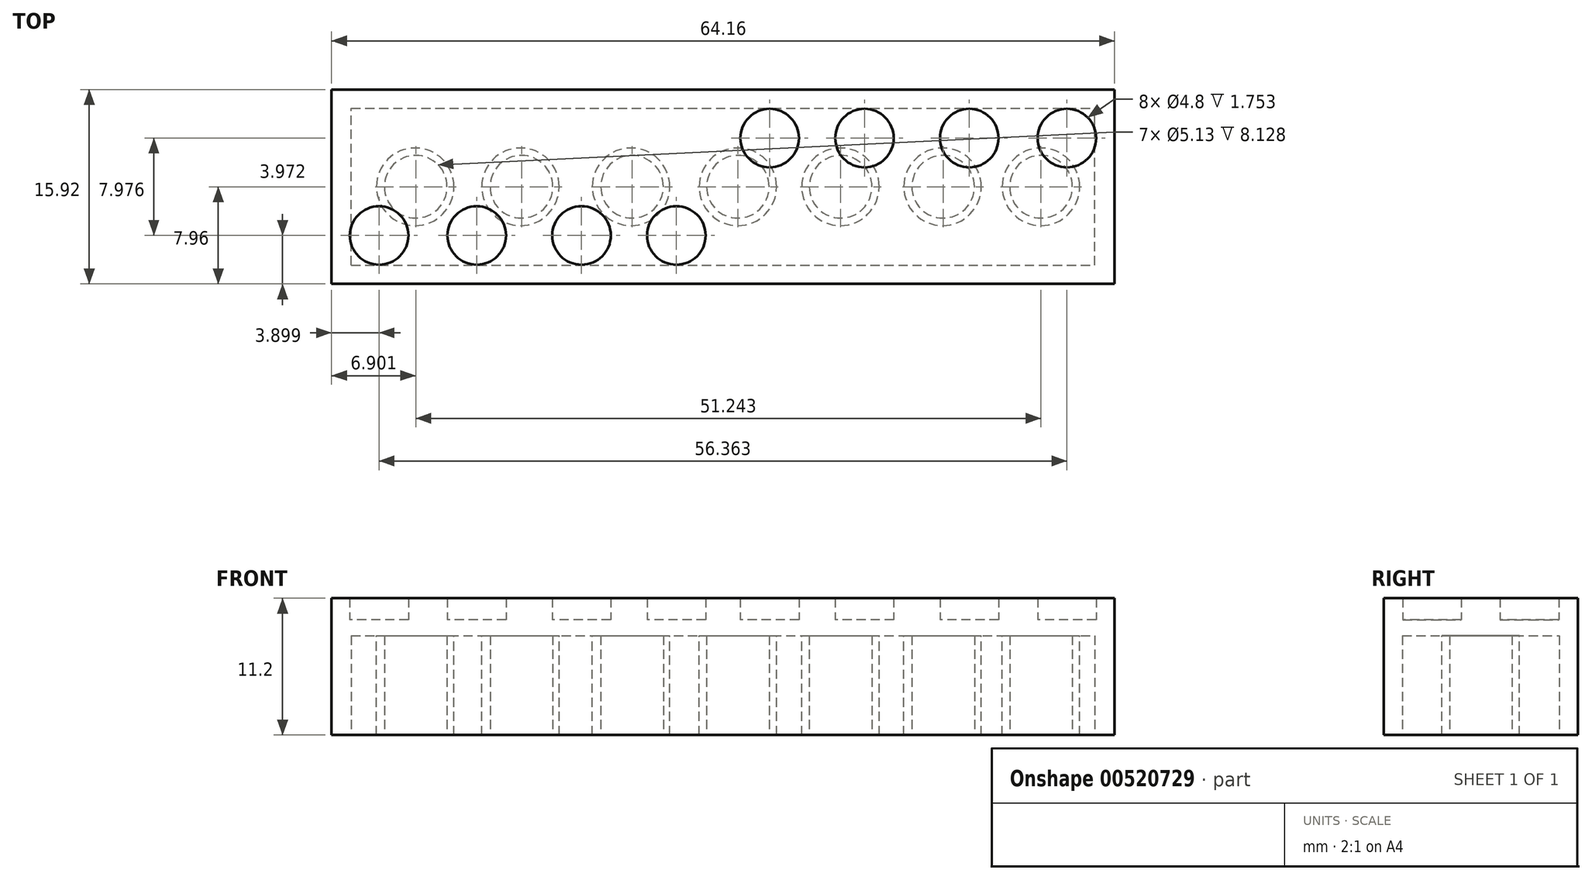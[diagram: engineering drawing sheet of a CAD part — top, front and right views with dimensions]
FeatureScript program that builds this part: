
annotation { "Feature Type Name" : "Feature", "Feature Type Description" : "" }
export const myFeature = defineFeature(function(context is Context, id is Id, definition is map)
    precondition{}
    {
        {
            var Q0;
            Q0=qCreatedBy(makeId("Top.planeOp"),FACE);
            var sketch = newSketch(context, id + "F0", { "sketchPlane" : qUnion([Q0])});
            skLineSegment(sketch, "E0.bottom", {"start": v(-32.08, 7.96) * mm, "end": v(32.08, 7.96) * mm});
            skLineSegment(sketch, "E0.top", {"start": v(-32.08, -7.96) * mm, "end": v(32.08, -7.96) * mm});
            skLineSegment(sketch, "E0.left", {"start": v(-32.08, 7.96) * mm, "end": v(-32.08, -7.96) * mm});
            skLineSegment(sketch, "E0.right", {"start": v(32.08, 7.96) * mm, "end": v(32.08, -7.96) * mm});
            skPoint(sketch, "E0.middle", {"position": v(0, 0) * mm});
            skSolve(sketch);
        }
        {
            var Q0;
            Q0=makeQuery(id+"F0.imprint","IMPRINT",FACE,{"disambiguationData":[TD([[makeQuery(id+"F0.imprint","IMPRINT",EDGE,{"derivedFrom":sQuery(id+"F0.wireOp",EDGE,"E0.bottom")}),-1.0]])]});
            extrude(context, id + "F1", {"entities" : qUnion([Q0]), "depth" : 9.45 * mm, "offsetDistance" : 25.4 * mm});
        }
        {
            var Q0;
            Q0=makeQuery(id+"F1.opExtrude","CAP_FACE",FACE,{"disambiguationData":[OSD([sQuery(id+"F0.wireOp",EDGE,"E0.bottom"),sQuery(id+"F0.wireOp",EDGE,"E0.top"),sQuery(id+"F0.wireOp",EDGE,"E0.left"),sQuery(id+"F0.wireOp",EDGE,"E0.right")])],"isStart":false});
            var sketch = newSketch(context, id + "F2", { "sketchPlane" : qUnion([Q0])});
            skCircle(sketch, "E1", {"center": v(-28.18, 3.99) * mm, "radius": 2.4 * mm});
            skCircle(sketch, "E2", {"center": v(-20.18, 3.99) * mm, "radius": 2.4 * mm});
            skCircle(sketch, "E3", {"center": v(-11.6, 3.99) * mm, "radius": 2.4 * mm});
            skCircle(sketch, "E4", {"center": v(-3.82, 3.99) * mm, "radius": 2.4 * mm});
            skCircle(sketch, "E5.MirrorC", {"center": v(3.82, 3.99) * mm, "radius": 2.4 * mm});
            skCircle(sketch, "E6.MirrorC", {"center": v(11.6, 3.99) * mm, "radius": 2.4 * mm});
            skCircle(sketch, "E7.MirrorC", {"center": v(20.18, 3.99) * mm, "radius": 2.4 * mm});
            skCircle(sketch, "E8.MirrorC", {"center": v(28.18, 3.99) * mm, "radius": 2.4 * mm});
            skCircle(sketch, "E9.MirrorC", {"center": v(28.18, -3.99) * mm, "radius": 2.4 * mm});
            skCircle(sketch, "E10.MirrorC", {"center": v(20.18, -3.99) * mm, "radius": 2.4 * mm});
            skCircle(sketch, "E11.MirrorC", {"center": v(11.6, -3.99) * mm, "radius": 2.4 * mm});
            skCircle(sketch, "E12.MirrorC", {"center": v(3.82, -3.99) * mm, "radius": 2.4 * mm});
            skCircle(sketch, "E13.MirrorC", {"center": v(-3.82, -3.99) * mm, "radius": 2.4 * mm});
            skCircle(sketch, "E14.MirrorC", {"center": v(-11.6, -3.99) * mm, "radius": 2.4 * mm});
            skCircle(sketch, "E15.MirrorC", {"center": v(-20.18, -3.99) * mm, "radius": 2.4 * mm});
            skCircle(sketch, "E16.MirrorC", {"center": v(-28.18, -3.99) * mm, "radius": 2.4 * mm});
            skSolve(sketch);
        }
        {
            var Q0;
            Q0=makeQuery(id+"F2.imprint","IMPRINT",FACE,{"disambiguationData":[TD([[makeQuery(id+"F2.imprint","IMPRINT",EDGE,{"derivedFrom":sQuery(id+"F2.wireOp",EDGE,"E16.MirrorC")}),-1.0]])]});
            var Q1;
            Q1=makeQuery(id+"F2.imprint","IMPRINT",FACE,{"disambiguationData":[TD([[makeQuery(id+"F2.imprint","IMPRINT",EDGE,{"derivedFrom":sQuery(id+"F2.wireOp",EDGE,"E15.MirrorC")}),-1.0]])]});
            var Q2;
            Q2=makeQuery(id+"F2.imprint","IMPRINT",FACE,{"disambiguationData":[TD([[makeQuery(id+"F2.imprint","IMPRINT",EDGE,{"derivedFrom":sQuery(id+"F2.wireOp",EDGE,"E14.MirrorC")}),-1.0]])]});
            var Q3;
            Q3=makeQuery(id+"F2.imprint","IMPRINT",FACE,{"disambiguationData":[TD([[makeQuery(id+"F2.imprint","IMPRINT",EDGE,{"derivedFrom":sQuery(id+"F2.wireOp",EDGE,"E13.MirrorC")}),-1.0]])]});
            var Q4;
            Q4=makeQuery(id+"F2.imprint","IMPRINT",FACE,{"disambiguationData":[TD([[makeQuery(id+"F2.imprint","IMPRINT",EDGE,{"derivedFrom":sQuery(id+"F2.wireOp",EDGE,"E12.MirrorC")}),1.0]])]});
            var Q5;
            Q5=makeQuery(id+"F2.imprint","IMPRINT",FACE,{"disambiguationData":[TD([[makeQuery(id+"F2.imprint","IMPRINT",EDGE,{"derivedFrom":sQuery(id+"F2.wireOp",EDGE,"E11.MirrorC")}),1.0]])]});
            var Q6;
            Q6=makeQuery(id+"F2.imprint","IMPRINT",FACE,{"disambiguationData":[TD([[makeQuery(id+"F2.imprint","IMPRINT",EDGE,{"derivedFrom":sQuery(id+"F2.wireOp",EDGE,"E10.MirrorC")}),1.0]])]});
            var Q7;
            Q7=makeQuery(id+"F2.imprint","IMPRINT",FACE,{"disambiguationData":[TD([[makeQuery(id+"F2.imprint","IMPRINT",EDGE,{"derivedFrom":sQuery(id+"F2.wireOp",EDGE,"E9.MirrorC")}),1.0]])]});
            var Q8;
            Q8=makeQuery(id+"F2.imprint","IMPRINT",FACE,{"disambiguationData":[TD([[makeQuery(id+"F2.imprint","IMPRINT",EDGE,{"derivedFrom":sQuery(id+"F2.wireOp",EDGE,"E8.MirrorC")}),-1.0]])]});
            var Q9;
            Q9=makeQuery(id+"F2.imprint","IMPRINT",FACE,{"disambiguationData":[TD([[makeQuery(id+"F2.imprint","IMPRINT",EDGE,{"derivedFrom":sQuery(id+"F2.wireOp",EDGE,"E7.MirrorC")}),-1.0]])]});
            var Q10;
            Q10=makeQuery(id+"F2.imprint","IMPRINT",FACE,{"disambiguationData":[TD([[makeQuery(id+"F2.imprint","IMPRINT",EDGE,{"derivedFrom":sQuery(id+"F2.wireOp",EDGE,"E6.MirrorC")}),-1.0]])]});
            var Q11;
            Q11=makeQuery(id+"F2.imprint","IMPRINT",FACE,{"disambiguationData":[TD([[makeQuery(id+"F2.imprint","IMPRINT",EDGE,{"derivedFrom":sQuery(id+"F2.wireOp",EDGE,"E5.MirrorC")}),-1.0]])]});
            var Q12;
            Q12=makeQuery(id+"F2.imprint","IMPRINT",FACE,{"disambiguationData":[TD([[makeQuery(id+"F2.imprint","IMPRINT",EDGE,{"derivedFrom":sQuery(id+"F2.wireOp",EDGE,"E4")}),1.0]])]});
            var Q13;
            Q13=makeQuery(id+"F2.imprint","IMPRINT",FACE,{"disambiguationData":[TD([[makeQuery(id+"F2.imprint","IMPRINT",EDGE,{"derivedFrom":sQuery(id+"F2.wireOp",EDGE,"E3")}),1.0]])]});
            var Q14;
            Q14=makeQuery(id+"F2.imprint","IMPRINT",FACE,{"disambiguationData":[TD([[makeQuery(id+"F2.imprint","IMPRINT",EDGE,{"derivedFrom":sQuery(id+"F2.wireOp",EDGE,"E2")}),1.0]])]});
            var Q15;
            Q15=makeQuery(id+"F2.imprint","IMPRINT",FACE,{"disambiguationData":[TD([[makeQuery(id+"F2.imprint","IMPRINT",EDGE,{"derivedFrom":sQuery(id+"F2.wireOp",EDGE,"E1")}),1.0]])]});
            extrude(context, id + "F3", {"entities" : qUnion([Q0, Q1, Q2, Q3, Q4, Q5, Q6, Q7, Q8, Q9, Q10, Q11, Q12, Q13, Q14, Q15]), "operationType" : NewBodyOperationType.ADD, "depth" : 1.75 * mm, "offsetDistance" : 25.4 * mm});
        }
        {
            var Q0;
            Q0=makeQuery(id+"F1.opExtrude","CAP_FACE",FACE,{"disambiguationData":[OSD([sQuery(id+"F0.wireOp",EDGE,"E0.bottom"),sQuery(id+"F0.wireOp",EDGE,"E0.top"),sQuery(id+"F0.wireOp",EDGE,"E0.left"),sQuery(id+"F0.wireOp",EDGE,"E0.right")])],"isStart":true});
            var sketch = newSketch(context, id + "F4", { "sketchPlane" : qUnion([Q0])});
            skLineSegment(sketch, "E17.bottom", {"start": v(-30.47, 6.43) * mm, "end": v(30.47, 6.43) * mm});
            skLineSegment(sketch, "E17.top", {"start": v(-30.47, -6.43) * mm, "end": v(30.47, -6.43) * mm});
            skLineSegment(sketch, "E17.left", {"start": v(-30.47, 6.43) * mm, "end": v(-30.47, -6.43) * mm});
            skLineSegment(sketch, "E17.right", {"start": v(30.47, 6.43) * mm, "end": v(30.47, -6.43) * mm});
            skPoint(sketch, "E17.middle", {"position": v(0, 0) * mm});
            skSolve(sketch);
        }
        {
            var Q0;
            Q0=makeQuery(id+"F4.imprint","IMPRINT",FACE,{"disambiguationData":[TD([[makeQuery(id+"F4.imprint","IMPRINT",EDGE,{"derivedFrom":sQuery(id+"F4.wireOp",EDGE,"E17.bottom")}),-1.0]])]});
            extrude(context, id + "F5", {"entities" : qUnion([Q0]), "operationType" : NewBodyOperationType.REMOVE, "oppositeDirection" : true, "depth" : 8.13 * mm, "offsetDistance" : 25.4 * mm});
        }
        {
            var Q0;
            Q0=makeQuery(id+"F5.boolean.opBoolean","COPY",FACE,{"derivedFrom":makeQuery(id+"F5.opExtrude","CAP_FACE",FACE,{"disambiguationData":[OSD([sQuery(id+"F4.wireOp",EDGE,"E17.bottom"),sQuery(id+"F4.wireOp",EDGE,"E17.top"),sQuery(id+"F4.wireOp",EDGE,"E17.left"),sQuery(id+"F4.wireOp",EDGE,"E17.right")])],"isStart":false})});
            var sketch = newSketch(context, id + "F6", { "sketchPlane" : qUnion([Q0])});
            skCircle(sketch, "E18", {"center": v(-25.22, 0) * mm, "radius": 3.18 * mm});
            skCircle(sketch, "E19", {"center": v(-16.6, 0) * mm, "radius": 3.18 * mm});
            skCircle(sketch, "E20", {"center": v(-7.53, 0) * mm, "radius": 3.18 * mm});
            skCircle(sketch, "E21", {"center": v(1.22, 0) * mm, "radius": 3.18 * mm});
            skCircle(sketch, "E22", {"center": v(9.62, 0) * mm, "radius": 3.18 * mm});
            skCircle(sketch, "E23", {"center": v(18, 0) * mm, "radius": 3.18 * mm});
            skCircle(sketch, "E24", {"center": v(26.06, 0) * mm, "radius": 3.18 * mm});
            skSolve(sketch);
        }
        {
            var Q0;
            Q0=makeQuery(id+"F6.imprint","IMPRINT",FACE,{"disambiguationData":[TD([[makeQuery(id+"F6.imprint","IMPRINT",EDGE,{"derivedFrom":sQuery(id+"F6.wireOp",EDGE,"E18")}),1.0]])]});
            var Q1;
            Q1=makeQuery(id+"F6.imprint","IMPRINT",FACE,{"disambiguationData":[TD([[makeQuery(id+"F6.imprint","IMPRINT",EDGE,{"derivedFrom":sQuery(id+"F6.wireOp",EDGE,"E19")}),1.0]])]});
            var Q2;
            Q2=makeQuery(id+"F6.imprint","IMPRINT",FACE,{"disambiguationData":[TD([[makeQuery(id+"F6.imprint","IMPRINT",EDGE,{"derivedFrom":sQuery(id+"F6.wireOp",EDGE,"E20")}),1.0]])]});
            var Q3;
            Q3=makeQuery(id+"F6.imprint","IMPRINT",FACE,{"disambiguationData":[TD([[makeQuery(id+"F6.imprint","IMPRINT",EDGE,{"derivedFrom":sQuery(id+"F6.wireOp",EDGE,"E21")}),1.0]])]});
            var Q4;
            Q4=makeQuery(id+"F6.imprint","IMPRINT",FACE,{"disambiguationData":[TD([[makeQuery(id+"F6.imprint","IMPRINT",EDGE,{"derivedFrom":sQuery(id+"F6.wireOp",EDGE,"E22")}),1.0]])]});
            var Q5;
            Q5=makeQuery(id+"F6.imprint","IMPRINT",FACE,{"disambiguationData":[TD([[makeQuery(id+"F6.imprint","IMPRINT",EDGE,{"derivedFrom":sQuery(id+"F6.wireOp",EDGE,"E23")}),1.0]])]});
            var Q6;
            Q6=makeQuery(id+"F6.imprint","IMPRINT",FACE,{"disambiguationData":[TD([[makeQuery(id+"F6.imprint","IMPRINT",EDGE,{"derivedFrom":sQuery(id+"F6.wireOp",EDGE,"E24")}),1.0]])]});
            extrude(context, id + "F7", {"entities" : qUnion([Q0, Q1, Q2, Q3, Q4, Q5, Q6]), "operationType" : NewBodyOperationType.ADD, "depth" : 8.13 * mm, "offsetDistance" : 25.4 * mm});
        }
        {
            var Q0;
            Q0=makeQuery(id+"F7.opExtrude","CAP_FACE",FACE,{"disambiguationData":[OSD([sQuery(id+"F6.wireOp",EDGE,"E21")])],"isStart":false});
            var sketch = newSketch(context, id + "F8", { "sketchPlane" : qUnion([Q0])});
            skCircle(sketch, "E25", {"center": v(-25.18, 0) * mm, "radius": 2.57 * mm});
            skCircle(sketch, "E26", {"center": v(-16.51, 0) * mm, "radius": 2.57 * mm});
            skCircle(sketch, "E27", {"center": v(-7.45, 0) * mm, "radius": 2.57 * mm});
            skCircle(sketch, "E28", {"center": v(1.22, 0) * mm, "radius": 2.57 * mm});
            skCircle(sketch, "E29", {"center": v(9.64, 0) * mm, "radius": 2.57 * mm});
            skCircle(sketch, "E30", {"center": v(18.04, 0) * mm, "radius": 2.57 * mm});
            skCircle(sketch, "E31", {"center": v(26.06, 0) * mm, "radius": 2.57 * mm});
            skSolve(sketch);
        }
        {
            var Q0;
            Q0=makeQuery(id+"F8.imprint","IMPRINT",FACE,{"disambiguationData":[TD([[makeQuery(id+"F8.imprint","IMPRINT",EDGE,{"derivedFrom":sQuery(id+"F8.wireOp",EDGE,"E25")}),1.0]])]});
            var Q1;
            Q1=makeQuery(id+"F8.imprint","IMPRINT",FACE,{"disambiguationData":[TD([[makeQuery(id+"F8.imprint","IMPRINT",EDGE,{"derivedFrom":sQuery(id+"F8.wireOp",EDGE,"E26")}),1.0]])]});
            var Q2;
            Q2=makeQuery(id+"F8.imprint","IMPRINT",FACE,{"disambiguationData":[TD([[makeQuery(id+"F8.imprint","IMPRINT",EDGE,{"derivedFrom":sQuery(id+"F8.wireOp",EDGE,"E27")}),1.0]])]});
            var Q3;
            Q3=makeQuery(id+"F8.imprint","IMPRINT",FACE,{"disambiguationData":[TD([[makeQuery(id+"F8.imprint","IMPRINT",EDGE,{"derivedFrom":sQuery(id+"F8.wireOp",EDGE,"E28")}),1.0]])]});
            var Q4;
            Q4=makeQuery(id+"F8.imprint","IMPRINT",FACE,{"disambiguationData":[TD([[makeQuery(id+"F8.imprint","IMPRINT",EDGE,{"derivedFrom":sQuery(id+"F8.wireOp",EDGE,"E29")}),1.0]])]});
            var Q5;
            Q5=makeQuery(id+"F8.imprint","IMPRINT",FACE,{"disambiguationData":[TD([[makeQuery(id+"F8.imprint","IMPRINT",EDGE,{"derivedFrom":sQuery(id+"F8.wireOp",EDGE,"E30")}),1.0]])]});
            var Q6;
            Q6=makeQuery(id+"F8.imprint","IMPRINT",FACE,{"disambiguationData":[TD([[makeQuery(id+"F8.imprint","IMPRINT",EDGE,{"derivedFrom":sQuery(id+"F8.wireOp",EDGE,"E31")}),1.0]])]});
            extrude(context, id + "F9", {"entities" : qUnion([Q0, Q1, Q2, Q3, Q4, Q5, Q6]), "operationType" : NewBodyOperationType.REMOVE, "oppositeDirection" : true, "depth" : 8.13 * mm, "offsetDistance" : 25.4 * mm});
        }
    });
